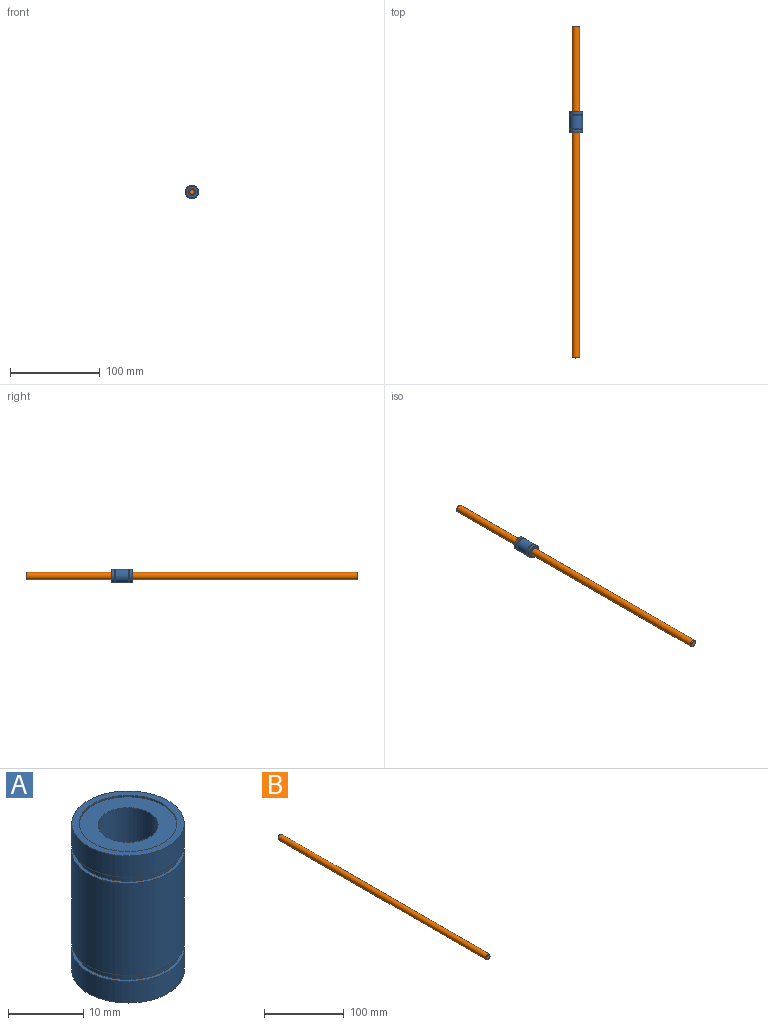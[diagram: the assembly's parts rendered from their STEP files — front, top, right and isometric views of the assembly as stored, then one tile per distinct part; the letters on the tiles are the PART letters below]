
ASSEMBLY  parts=2 mates=1
PART A: 16 faces, bbox 15x15x24 mm
  f0: plane 13x13mm, normal (0,0,1), area 82.5mm2, adj f1,f15
  f1: cylinder r=6.5mm len=13mm, axis (0,0,1), area 10.2mm2, adj f0,f2
  f2: plane 15x15mm, normal (0,0,1), area 44mm2, adj f1,f3
  f3: cylinder r=7.5mm len=15mm, axis (0,0,1), area 164.9mm2, adj f2,f4
  f4: plane 15x15mm, normal (0,0,-1), area 22.8mm2, adj f3,f5
  f5: cylinder r=7mm len=14mm, axis (0,0,1), area 44mm2, adj f4,f6
  f6: plane 15x15mm, normal (0,0,1), area 22.8mm2, adj f5,f7
  f7: cylinder r=7.5mm len=15mm, axis (0,0,1), area 706.9mm2, adj f6,f8
  f8: plane 15x15mm, normal (0,0,-1), area 22.8mm2, adj f7,f9
  f9: cylinder r=7mm len=14mm, axis (0,0,1), area 44mm2, adj f8,f10
  f10: plane 15x15mm, normal (0,0,1), area 22.8mm2, adj f9,f11
  f11: cylinder r=7.5mm len=15mm, axis (0,0,1), area 164.9mm2, adj f10,f12
  f12: plane 15x15mm, normal (0,0,-1), area 44mm2, adj f11,f13
  f13: cylinder r=6.5mm len=13mm, axis (0,0,1), area 10.2mm2, adj f12,f14
  f14: plane 13x13mm, normal (0,0,-1), area 82.5mm2, adj f13,f15
  f15: cylinder r=4mm len=23.5mm, axis (0,0,1), area 590.6mm2, adj f0,f14
PART B: 5 faces, bbox 8x370x8 mm
  f0: cylinder r=4mm len=368mm, axis (0,1,0), area 9248.8mm2, adj f3,f4
  f1: plane 6x6mm, normal (0,-1,0), area 28.3mm2, adj f4
  f2: plane 6x6mm, normal (0,1,0), area 28.3mm2, adj f3
  f3: cone r=4mm half-angle=45deg, axis (0,-1,0), area 31.1mm2, adj f0,f2
  f4: cone r=3mm half-angle=45deg, axis (0,1,0), area 31.1mm2, adj f0,f1
PLACE A rot(axis=(-1,0,0),90deg) t=(0,-107.01,0)mm
PLACE B at identity fixed
MATE slider A.f1 <-> B.f0  axis (0,1,0) through (0,-95.26,0)mm
